# Revit family: BoelsRental_TelescopicBoomLift_SKYJACK_SJ45Ta
name_source: partatom
category: Site
units: mm (PartAtom-declared; Revit-internal decimal feet)

## family parameters
Always vertical = Yes
Cut with Voids When Loaded = No
OmniClass Number = 23.50.85.17
OmniClass Title = Telescoping Platforms
Part Type = Normal
Round Connector Dimension = Use Diameter
Shared = No
Work Plane-Based = No

## types (1)
- SJ45T
    Assembly Code = E1030100
    AssetType = Movable
    AxleOscillation = 7.62 cm
    BIMObjectName = BoelsRental_TelescopicBoomLift_SKYJACK_SJ45T
    BoelsSubgroup = 18039 - Telescopic boom lift 15.8m
    BoomAngle(Max) = 77.50°
    BoomAngle(Min) = -12.50°
    Capacity = 227 kg
    ClassificationName = Uniclass2015
    ClassificationValue = Pr_65_80_47_95
    Cost = 0 $
    Description = TELESCOPIC BOOM LIFT, DIESEL <14m
    DocumentationCertificates = https://www.boels.com
    DocumentationInstallationGuide = https://www.boels.com
    DocumentationLiterature = https://www.boels.com
    DocumentationMaintenance = https://www.boels.com
    DocumentationTechnical = https://www.boels.com
    DurationUnit = Years
    Engine = 55.2 kw (74 HP)
    ExpectedLife = 0
    FuelTankCapacity = 170 L
    Gradeability = 50%
    GroundClearance = 280 mm
    HorizontalReach = 12 mm  [stored 0.0393701 ft]
    HydraulicReservoir = 227 L
    IfcExportAs = IfcTransportElement
    IfcExportType = IfcTransportElementType
    InsideTurningRadius = 2.82 m
    JibAngle(Max) = 65.00°
    JibAngle(Min) = -60.00°
    JibLength = 1.52 m
    JibRange = +65° / -60°
    Keynote = X
    LocalFloorLoadWithRatedLoad = 1,140 kPa
    Manufacturer = Boels Rental (SKYJACK)
    ManufacturerName = Boels Rental (SKYJACK)
    Material = Steel
    MaximumNumberOfPersons = 2
    Model = Telescopic Boom Lift - SJ45T
    ModelNumber = SJ45T
    ModelReference = Telescopic Boom Lift
    NBSDescription = Vertical lifting platforms
    NBSObjectName = Boels Rental - Vertical lifting platforms
    NBSReference = 90-80-65/350
    NominalDepth = 0 mm  [stored 0 ft]
    NominalHeight = 0 mm  [stored 0 ft]
    NominalLength = 0 mm  [stored 0 ft]
    OutsideTurningRadius = 5.05 m
    OverallFloorLoadWithRatedLoad = 17.8 kPa
    OverallHeight = 2390 mm
    OverallLength = 8790 mm
    OverallWidth = 2290 mm
    PlatformHeight = 13770 mm
    PlatformRotation = 170°
    PlatformRotationAngle(Max) = 85.00°
    PlatformRotationAngle(Min) = -85.00°
    PlatformSize = 0.91 x 1.83 m
    ProductPageLink = https://www.boels.com
    ProductionYear = 2022
    Rotation = 360° Continuous
    Tailswing = 940 mm
    TelescopicExtension(Max) = 4400 mm
    TelescopicExtension(Min) = 0 mm  [stored 0 ft]
    TireSize = 15 x 19.5
    TireType = Grip lug foam-filled
    Type Comments = Telescopic Boom Lift - SJ45T
    TypeName = Telescopic Boom Lift - SJ45T
    URL = https://www.boels.com
    WarrantyDurationLabor = 0
    WarrantyDurationParts = 0
    WarrantyDurationUnit = Years
    WarrantyGuarantorLabor = https://www.boels.com
    WarrantyGuarantorParts = https://www.boels.com
    Weight = 12,800 kg
    Wheelbase = 2440 mm
    WorkingHeight = 15770 mm
    _BSBibleVersion = 16
    _BimSpecGuid = 0
    _CurrentRevision = 1
    _DistributedBy = https://www.boels.com
    _ObjectUserGuide = https://www.boels.com

note: [stored X ft] marks values corroborated as IEEE doubles in the binary element streams (Revit-internal decimal feet)

## geometry (parser evidence)
native form markers: Sweep x33
no freeform markers — native parametric forms only
